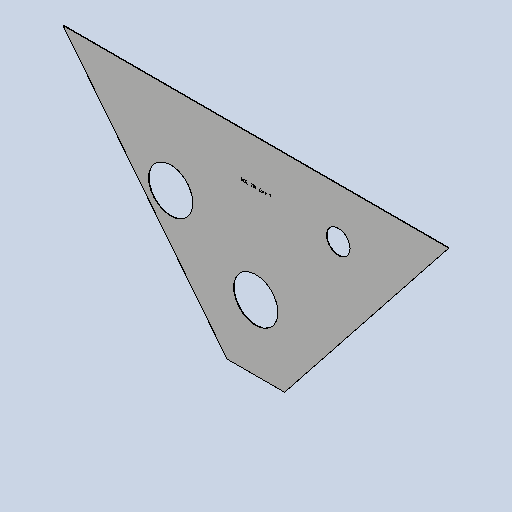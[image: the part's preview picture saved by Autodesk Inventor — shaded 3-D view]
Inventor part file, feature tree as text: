
AUTODESK INVENTOR PART (.ipt)
format: ipt  version: 2025 (Build 290162010, 162A)  size: 232,448 bytes
history: native  units: mm
features: other x6, sketch x3, sheet_metal_op x1, mirror x1, extrude x1, projected_geometry x1, reference x1
ambient origin geometry x8: Origin, YZ Plane, XZ Plane, XY Plane, X Axis, Y Axis, Z Axis, Center Point
bodies: Solid1 (feature_tree)
feature tree (14):
  sheet_metal_op  "Face1"
  mirror  "Mirror1"
  extrude  "Extrusion1"  Depth=2.0mm
  other  "Mark1"
  sketch  "Sketch1"  dims[d1=735.090647mm d2=2.0mm]
  other  "Plate1"
  sketch  "Sketch2"  dims[d3=2.0mm]
  projected_geometry  "Projected Loop1"
  sketch  "Sketch3"  dims[d5=22.414154mm d6=110.0mm d9=790.0mm d13=169.0mm d14=0.0mm d15=0.0mm d16=250.0mm d17=450.0mm d18=325.0mm d19=31.0mm d20=90.0mm d21=156.0mm d23=315.0mm d24=600.0mm d25=12.0mm d26=110.0mm d27=50.0mm d28=22.414154mm]
  reference  "Reference2"
  other  "Definition1"
  other  "ASY MSC 001 отстойник осветлитель.iam"
  other  "ASY MSC 204 BELLY.iam:1"
  other  "MSC 505 sheet belly-neck:1"
